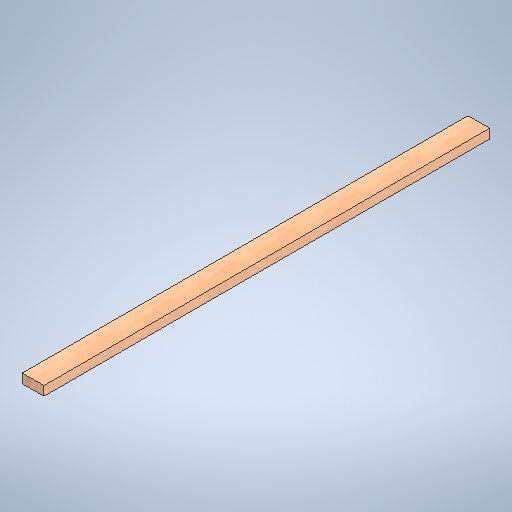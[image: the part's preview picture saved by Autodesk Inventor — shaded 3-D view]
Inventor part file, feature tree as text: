
AUTODESK INVENTOR PART (.ipt)
format: ipt  version: 2025 (Build 290162010, 162A)  size: 287,232 bytes
history: native  units: in
note: dims shown in document units (in); Inventor stores cm internally (conversion verified against a paired STEP export)
features: extrude x1, sketch x1
ambient origin geometry x8: Origin, YZ Plane, XZ Plane, XY Plane, X Axis, Y Axis, Z Axis, Center Point
bodies: Solid1 (feature_tree)
feature tree (2):
  extrude  "Extrusion1"  Depth=1.5in
  sketch  "Sketch1"  dims[d0=3.5in d1=1.5in d2=72.0in d3=0.0in]
